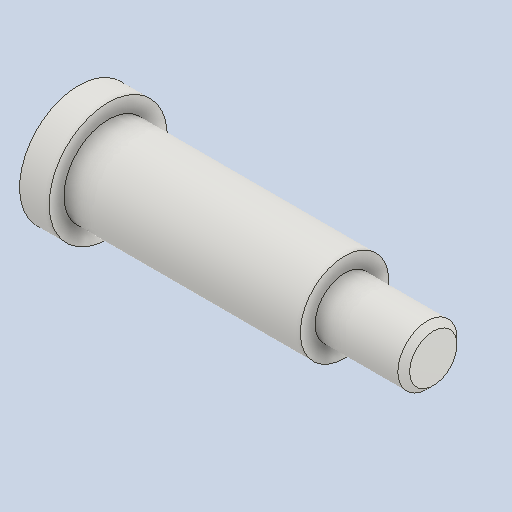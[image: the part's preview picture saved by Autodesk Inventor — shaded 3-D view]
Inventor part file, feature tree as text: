
AUTODESK INVENTOR PART (.ipt)
format: ipt  version: 2022 (Build 260153000, 153)  size: 121,344 bytes
history: native  units: mm
features: other x4, revolve x1, chamfer x1
ambient origin geometry x6: Origin, XZ Plane, XY Plane, X Axis, Y Axis, Z Axis
bodies: Body1 (feature_tree)
feature tree (6):
  other  "Твердое тело1"
  revolve  "Вращение1"
  chamfer  "Фаска1"  [1 undecoded]
  other  "Начальная плоскость"
  other  "Исходная точка"
  other  "Основной эскиз"
note: 1 required parameter value undecoded (feature->parameter linkage not recoverable at this tier; creation-order binding heuristic only, values carry confidence <= 0.55)
